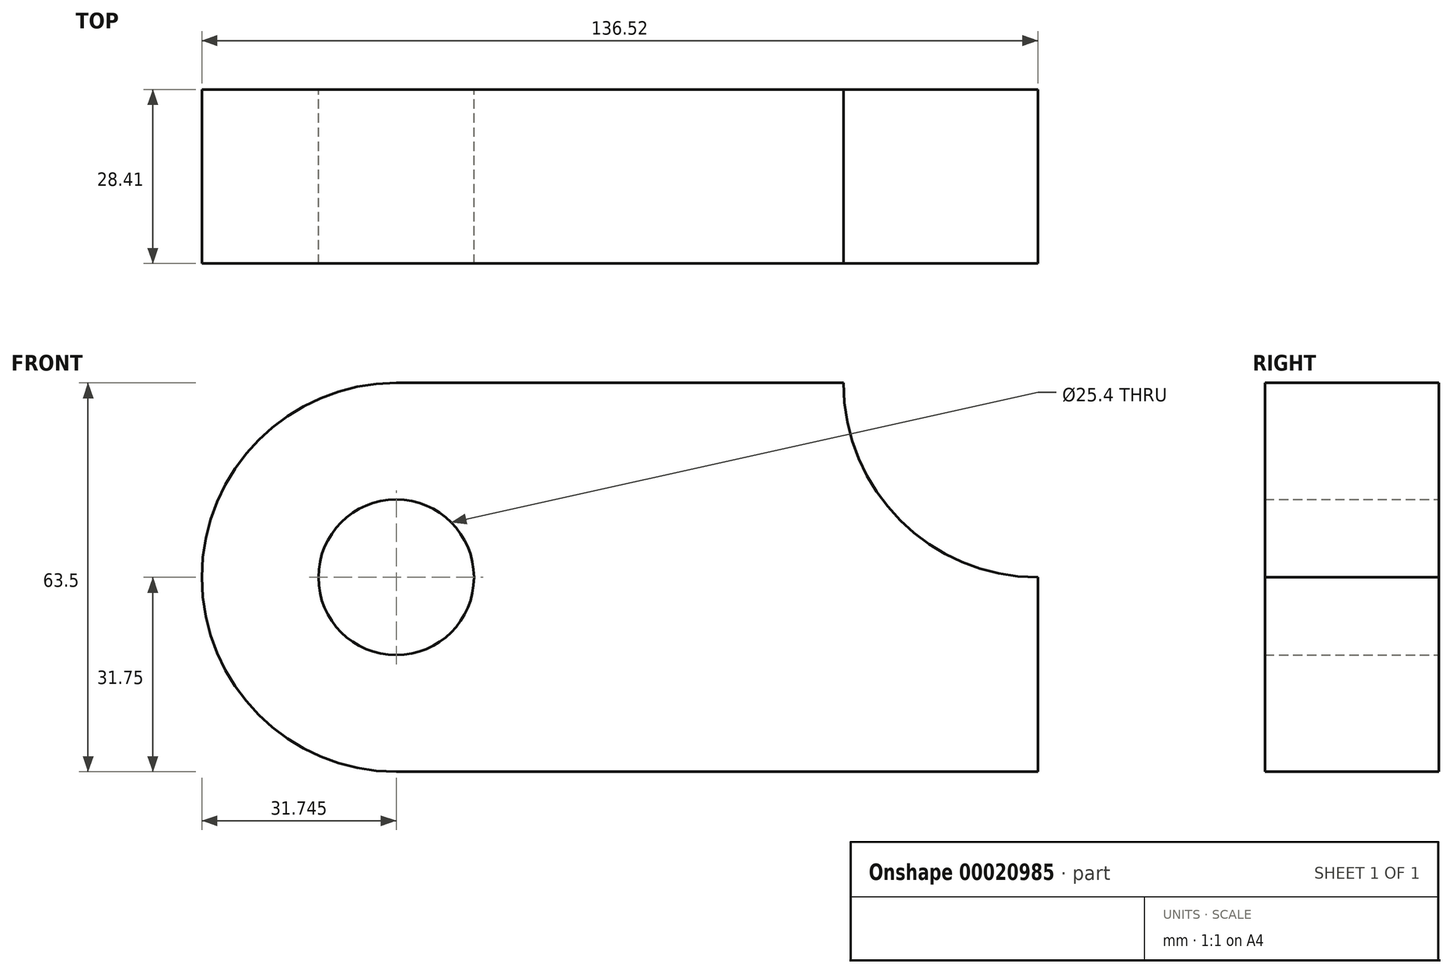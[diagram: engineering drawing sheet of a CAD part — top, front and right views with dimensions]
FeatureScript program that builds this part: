
annotation { "Feature Type Name" : "Feature", "Feature Type Description" : "" }
export const myFeature = defineFeature(function(context is Context, id is Id, definition is map)
    precondition{}
    {
        {
            var Q0;
            Q0=qCreatedBy(makeId("Front.planeOp"),FACE);
            var sketch = newSketch(context, id + "F0", { "sketchPlane" : qUnion([Q0])});
            skLineSegment(sketch, "E0.bottom", {"start": v(0, 0) * mm, "end": v(-104.77, 0) * mm});
            skLineSegment(sketch, "E0.top", {"start": v(0, 63.5) * mm, "end": v(-104.78, 63.5) * mm});
            skLineSegment(sketch, "E0.left", {"start": v(0, 0) * mm, "end": v(0, 63.5) * mm});
            skArc(sketch, "E1", {"start": v(-104.78, 63.5) * mm, "mid": v(-136.53, 31.75) * mm, "end": v(-104.78, 0) * mm});
            skCircle(sketch, "E2", {"center": v(-104.78, 31.75) * mm, "radius": 12.7 * mm});
            skArc(sketch, "E3", {"start": v(-31.75, 63.5) * mm, "mid": v(-22.45, 41.05) * mm, "end": v(0, 31.75) * mm});
            skSolve(sketch);
        }
        {
            var Q0;
            {var subQ3=sQuery(id+"F0.wireOp",EDGE,"E0.bottom");Q0=makeQuery(id+"F0.imprint","IMPRINT",FACE,{"disambiguationData":[TD([[makeQuery(id+"F0.imprint","IMPRINT",EDGE,{"derivedFrom":subQ3}),-1.0]])]});}
            extrude(context, id + "F1", {"entities" : qUnion([Q0]), "depth" : 28.41 * mm});
        }
    });
